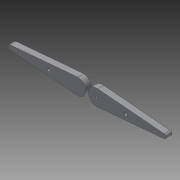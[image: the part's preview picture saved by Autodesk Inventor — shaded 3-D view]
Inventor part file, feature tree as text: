
AUTODESK INVENTOR PART (.ipt)
format: ipt  version: 2015 (Build 190159000, 159)  size: 90,624 bytes
history: native  units: in
note: dims shown in document units (in); Inventor stores cm internally (conversion verified against a paired STEP export)
features: extrude x1, sketch x1
ambient origin geometry x8: Origin, YZ Plane, XZ Plane, XY Plane, X Axis, Y Axis, Z Axis, Center Point
bodies: Solid1 (feature_tree)
feature tree (2):
  extrude  "Extrusion1"  Depth=0.1181in
  sketch  "Sketch1"  dims[d0=0.315in d1=0.315in d2=0.1181in d3=0.0in]
